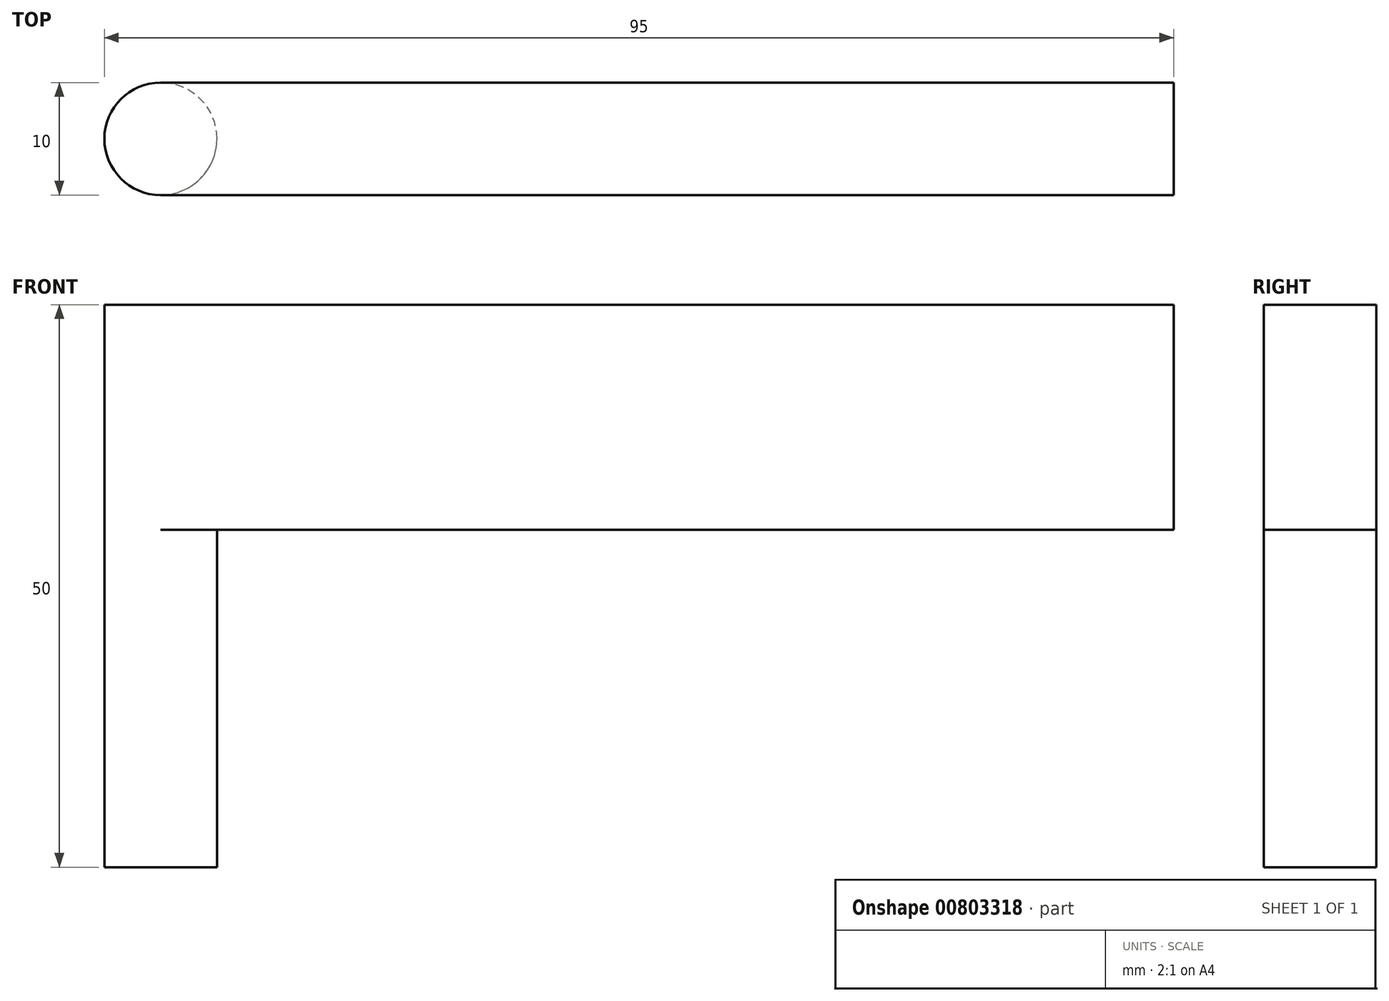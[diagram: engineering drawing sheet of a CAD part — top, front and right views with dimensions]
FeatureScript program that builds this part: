
annotation { "Feature Type Name" : "Feature", "Feature Type Description" : "" }
export const myFeature = defineFeature(function(context is Context, id is Id, definition is map)
    precondition{}
    {
        {
            var Q0;
            Q0=qCreatedBy(makeId("Front.planeOp"),FACE);
            var sketch = newSketch(context, id + "F0", { "sketchPlane" : qUnion([Q0])});
            skLineSegment(sketch, "E0", {"start": v(0, 0) * mm, "end": v(-5, 0) * mm});
            skLineSegment(sketch, "E1", {"start": v(-5, 0) * mm, "end": v(-5, 30) * mm});
            skLineSegment(sketch, "E2", {"start": v(0, 60) * mm, "end": v(0, 0) * mm});
            skLineSegment(sketch, "E3", {"start": v(-5, 30) * mm, "end": v(0, 30) * mm});
            skLineSegment(sketch, "E4", {"start": v(0, 30) * mm, "end": v(0, 0) * mm});
            skSolve(sketch);
        }
        {
            var Q0;
            Q0 = qSketchRegion(id + "F0", true);
            var Q1;
            Q1=sQuery(id+"F0.wireOp",EDGE,"E2");
            revolve(context, id + "F1", {"surfaceOperationType" : NewSurfaceOperationType.NEW, "entities" : qUnion([Q0]), "axis" : qUnion([Q1]), "revolveType" : RevolveType.FULL});
        }
        {
            var Q0;
            Q0=makeQuery(id+"F1.opRevolve","SWEPT_FACE",FACE,{"disambiguationData":[OSD([sQuery(id+"F0.wireOp",EDGE,"E3")])]});
            var sketch = newSketch(context, id + "F2", { "sketchPlane" : qUnion([Q0])});
            skArc(sketch, "E5", {"start": v(0, 5) * mm, "mid": v(-5, 0) * mm, "end": v(0, -5) * mm});
            skLineSegment(sketch, "E6", {"start": v(0, 5) * mm, "end": v(90, 5) * mm});
            skLineSegment(sketch, "E7", {"start": v(0, -5) * mm, "end": v(90, -5) * mm});
            skLineSegment(sketch, "E8", {"start": v(90, -5) * mm, "end": v(90, 5) * mm});
            skSolve(sketch);
        }
        {
            var Q0;
            Q0 = qSketchRegion(id + "F2", true);
            extrude(context, id + "F3", {"entities" : qUnion([Q0]), "operationType" : NewBodyOperationType.ADD, "depth" : 20 * mm, "offsetDistance" : 25 * mm});
        }
    });
